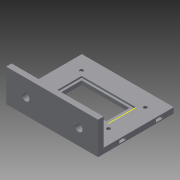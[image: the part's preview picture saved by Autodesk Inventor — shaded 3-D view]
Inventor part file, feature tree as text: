
AUTODESK INVENTOR PART (.ipt)
format: ipt  version: 2015 (Build 190159000, 159)  size: 201,728 bytes
history: native  units: in
note: dims shown in document units (in); Inventor stores cm internally (conversion verified against a paired STEP export)
features: sketch x10, extrude x9
ambient origin geometry x8: Origin, YZ Plane, XZ Plane, XY Plane, X Axis, Y Axis, Z Axis, Center Point
bodies: Solid1 (feature_tree)
feature tree (19):
  extrude  "Extrusion1"  Depth=3.3465in
  extrude  "Extrusion2"  TaperAngle=0.0deg  [1 undecoded]
  extrude  "Extrusion3"  Depth=0.1969in
  extrude  "Extrusion4"  Depth=0.685in
  extrude  "Extrusion9"  Depth=0.8622in
  sketch  "Sketch16"  dims[d18=0.0591in d19=0.0in d20=0.0787in]
  extrude  "Extrusion14"  Depth=0.0787in
  extrude  "Extrusion16"  Depth=0.0787in
  extrude  "Extrusion17"  Depth=0.0394in TaperAngle=0.0deg
  extrude  "Extrusion18"  Depth=0.6004in
  sketch  "Sketch1"  dims[d4=2.7559in d5=3.3465in]
  sketch  "Sketch2"  dims[d6=1.1811in d7=0.0in d8=0.0in]
  sketch  "Sketch3"  dims[d9=0.0in d10=0.1969in]
  sketch  "Sketch4"  dims[d12=0.9843in d13=0.0in d14=0.685in]
  sketch  "Sketch10"  dims[d15=0.685in d17=0.8622in]
  sketch  "Sketch17"  dims[d21=0.0787in d22=0.0787in]
  sketch  "Sketch20"  dims[d23=0.1575in d24=0.0394in d25=0.0in]
  sketch  "Sketch21"  dims[d53=0.6004in d55=0.6004in]
  sketch  "Sketch22"  dims[d58=0.2756in d59=0.2756in d60=0.1969in d61=0.0in d70=1.9291in d71=0.7087in d93=0.0in d94=0.0in d95=0.0in d96=0.0in d97=0.1969in d98=0.0in d106=1.0039in d107=0.128in d110=1.3386in d111=2.3228in d113=0.0984in d125=0.2362in d130=0.6299in d131=0.0in d136=0.6299in d137=0.0in d139=0.0541in d140=0.0541in d141=0.0in d142=0.0in]
note: 1 required parameter value undecoded (feature->parameter linkage not recoverable at this tier; creation-order binding heuristic only, values carry confidence <= 0.55)
